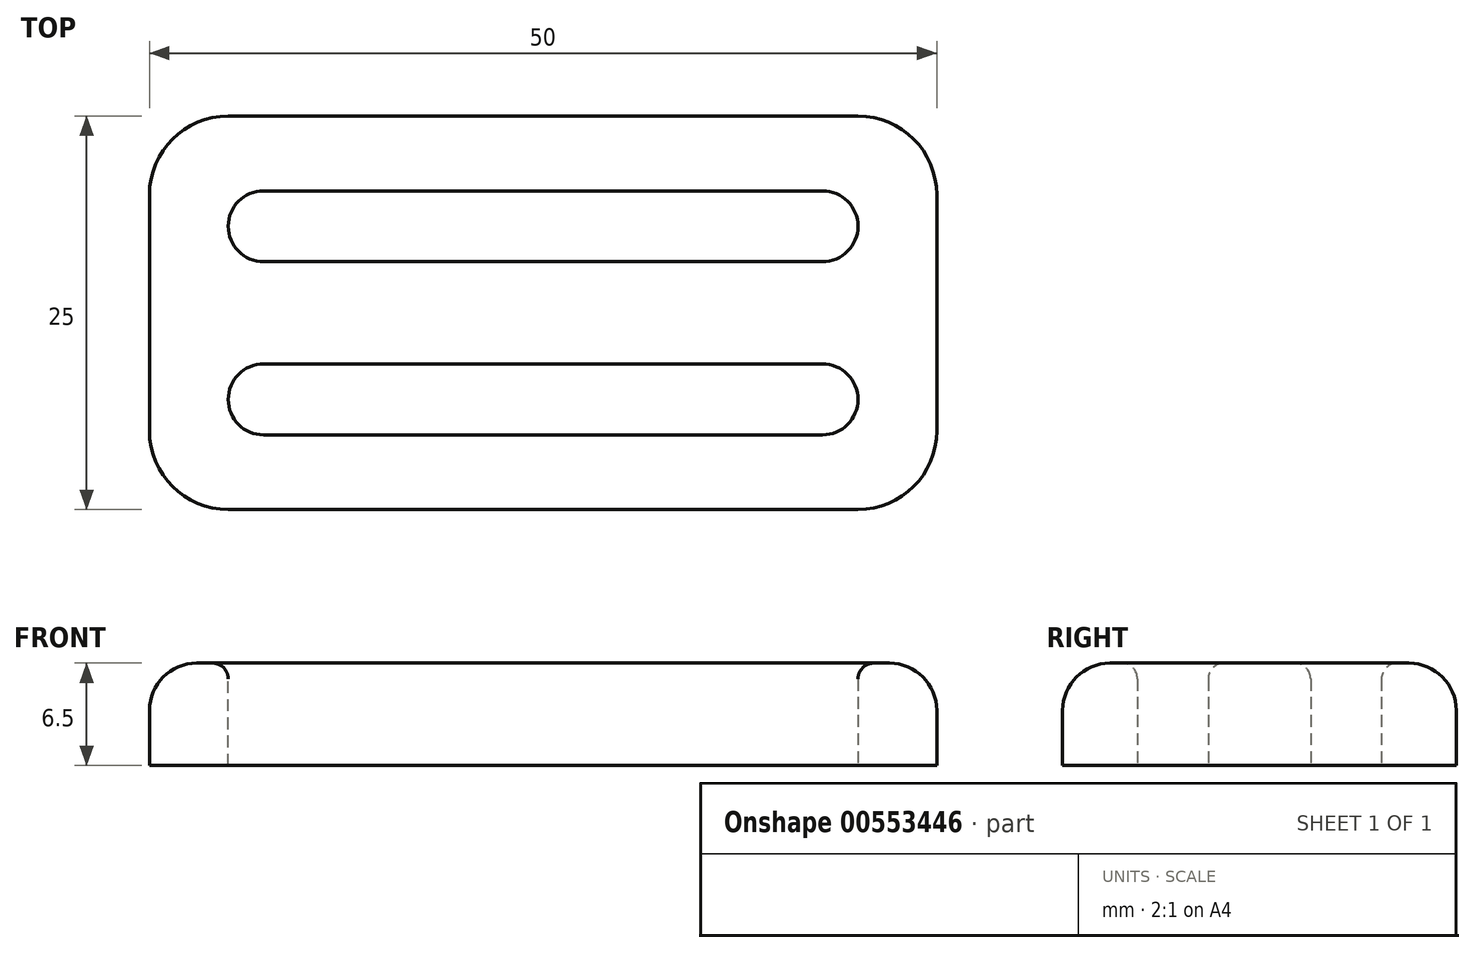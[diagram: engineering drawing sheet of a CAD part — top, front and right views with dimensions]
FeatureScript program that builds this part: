
annotation { "Feature Type Name" : "Feature", "Feature Type Description" : "" }
export const myFeature = defineFeature(function(context is Context, id is Id, definition is map)
    precondition{}
    {
        {
            var Q0;
            Q0=qCreatedBy(makeId("Top.planeOp"),FACE);
            var sketch = newSketch(context, id + "F0", { "sketchPlane" : qUnion([Q0])});
            skLineSegment(sketch, "E0.bottom", {"start": v(25, 12.5) * mm, "end": v(-25, 12.5) * mm});
            skLineSegment(sketch, "E0.top", {"start": v(25, -12.5) * mm, "end": v(-25, -12.5) * mm});
            skLineSegment(sketch, "E0.left", {"start": v(25, 12.5) * mm, "end": v(25, -12.5) * mm});
            skLineSegment(sketch, "E0.right", {"start": v(-25, 12.5) * mm, "end": v(-25, -12.5) * mm});
            skPoint(sketch, "E0.middle", {"position": v(0, 0) * mm});
            skLineSegment(sketch, "E1.bottom", {"start": v(20, 3.25) * mm, "end": v(-20, 3.25) * mm});
            skLineSegment(sketch, "E1.top", {"start": v(20, 7.75) * mm, "end": v(-20, 7.75) * mm});
            skLineSegment(sketch, "E1.left", {"start": v(20, 3.25) * mm, "end": v(20, 7.75) * mm});
            skLineSegment(sketch, "E1.right", {"start": v(-20, 3.25) * mm, "end": v(-20, 7.75) * mm});
            skPoint(sketch, "E1.middle", {"position": v(0, 5.5) * mm});
            skLineSegment(sketch, "E2.MirrorCS", {"start": v(20, -3.25) * mm, "end": v(-20, -3.25) * mm});
            skLineSegment(sketch, "E3.MirrorCS", {"start": v(-20, -3.25) * mm, "end": v(-20, -7.75) * mm});
            skLineSegment(sketch, "E4.MirrorCS", {"start": v(20, -3.25) * mm, "end": v(20, -7.75) * mm});
            skLineSegment(sketch, "E5.MirrorCS", {"start": v(20, -7.75) * mm, "end": v(-20, -7.75) * mm});
            skSolve(sketch);
        }
        {
            var Q0;
            Q0=makeQuery(id+"F0.imprint","IMPRINT",FACE,{"disambiguationData":[TD([[makeQuery(id+"F0.imprint","IMPRINT",EDGE,{"derivedFrom":sQuery(id+"F0.wireOp",EDGE,"E0.bottom")}),1.0]])]});
            extrude(context, id + "F1", {"entities" : qUnion([Q0]), "depth" : 6.5 * mm, "offsetDistance" : 25 * mm});
        }
        {
            var Q0;
            Q0=makeQuery(id+"F1.opExtrude","SWEPT_EDGE",EDGE,{"disambiguationData":[OSD([sQuery(id+"F0.wireOp",EDGE,"E0.top"),sQuery(id+"F0.wireOp",EDGE,"E0.right")])]});
            var Q1;
            Q1=makeQuery(id+"F1.opExtrude","SWEPT_EDGE",EDGE,{"disambiguationData":[OSD([sQuery(id+"F0.wireOp",EDGE,"E0.top"),sQuery(id+"F0.wireOp",EDGE,"E0.left")])]});
            var Q2;
            Q2=makeQuery(id+"F1.opExtrude","SWEPT_EDGE",EDGE,{"disambiguationData":[OSD([sQuery(id+"F0.wireOp",EDGE,"E0.bottom"),sQuery(id+"F0.wireOp",EDGE,"E0.left")])]});
            var Q3;
            Q3=makeQuery(id+"F1.opExtrude","SWEPT_EDGE",EDGE,{"disambiguationData":[OSD([sQuery(id+"F0.wireOp",EDGE,"E0.bottom"),sQuery(id+"F0.wireOp",EDGE,"E0.right")])]});
            fillet(context, id + "F2", {"entities" : qUnion([Q0, Q1, Q2, Q3]), "radius" : 5 * mm, "tangentPropagation" : true, "allowEdgeOverflow" : false});
        }
        {
            var Q0;
            Q0=makeQuery(id+"F1.opExtrude","SWEPT_EDGE",EDGE,{"disambiguationData":[OSD([sQuery(id+"F0.wireOp",EDGE,"E2.MirrorCS"),sQuery(id+"F0.wireOp",EDGE,"E3.MirrorCS")])]});
            var Q1;
            Q1=makeQuery(id+"F1.opExtrude","SWEPT_EDGE",EDGE,{"disambiguationData":[OSD([sQuery(id+"F0.wireOp",EDGE,"E3.MirrorCS"),sQuery(id+"F0.wireOp",EDGE,"E5.MirrorCS")])]});
            var Q2;
            Q2=makeQuery(id+"F1.opExtrude","SWEPT_EDGE",EDGE,{"disambiguationData":[OSD([sQuery(id+"F0.wireOp",EDGE,"E1.bottom"),sQuery(id+"F0.wireOp",EDGE,"E1.right")])]});
            var Q3;
            Q3=makeQuery(id+"F1.opExtrude","SWEPT_EDGE",EDGE,{"disambiguationData":[OSD([sQuery(id+"F0.wireOp",EDGE,"E1.top"),sQuery(id+"F0.wireOp",EDGE,"E1.right")])]});
            var Q4;
            Q4=makeQuery(id+"F1.opExtrude","SWEPT_EDGE",EDGE,{"disambiguationData":[OSD([sQuery(id+"F0.wireOp",EDGE,"E4.MirrorCS"),sQuery(id+"F0.wireOp",EDGE,"E5.MirrorCS")])]});
            var Q5;
            Q5=makeQuery(id+"F1.opExtrude","SWEPT_EDGE",EDGE,{"disambiguationData":[OSD([sQuery(id+"F0.wireOp",EDGE,"E2.MirrorCS"),sQuery(id+"F0.wireOp",EDGE,"E4.MirrorCS")])]});
            var Q6;
            Q6=makeQuery(id+"F1.opExtrude","SWEPT_EDGE",EDGE,{"disambiguationData":[OSD([sQuery(id+"F0.wireOp",EDGE,"E1.bottom"),sQuery(id+"F0.wireOp",EDGE,"E1.left")])]});
            var Q7;
            Q7=makeQuery(id+"F1.opExtrude","SWEPT_EDGE",EDGE,{"disambiguationData":[OSD([sQuery(id+"F0.wireOp",EDGE,"E1.top"),sQuery(id+"F0.wireOp",EDGE,"E1.left")])]});
            fillet(context, id + "F3", {"entities" : qUnion([Q0, Q1, Q2, Q3, Q4, Q5, Q6, Q7]), "radius" : 2.25 * mm, "tangentPropagation" : true, "allowEdgeOverflow" : false});
        }
        {
            var Q0;
            Q0=makeQuery(id+"F1.opExtrude","CAP_EDGE",EDGE,{"disambiguationData":[OSD([sQuery(id+"F0.wireOp",EDGE,"E5.MirrorCS")])],"isStart":false});
            var Q1;
            Q1=makeQuery(id+"F1.opExtrude","CAP_EDGE",EDGE,{"disambiguationData":[OSD([sQuery(id+"F0.wireOp",EDGE,"E1.bottom")])],"isStart":false});
            fillet(context, id + "F4", {"entities" : qUnion([Q0, Q1]), "radius" : 1 * mm, "tangentPropagation" : true, "allowEdgeOverflow" : false});
        }
        {
            var Q0;
            Q0=makeQuery(id+"F1.opExtrude","CAP_EDGE",EDGE,{"disambiguationData":[OSD([sQuery(id+"F0.wireOp",EDGE,"E0.left")])],"isStart":false});
            fillet(context, id + "F5", {"entities" : qUnion([Q0]), "radius" : 3 * mm, "tangentPropagation" : true, "allowEdgeOverflow" : false});
        }
    });
